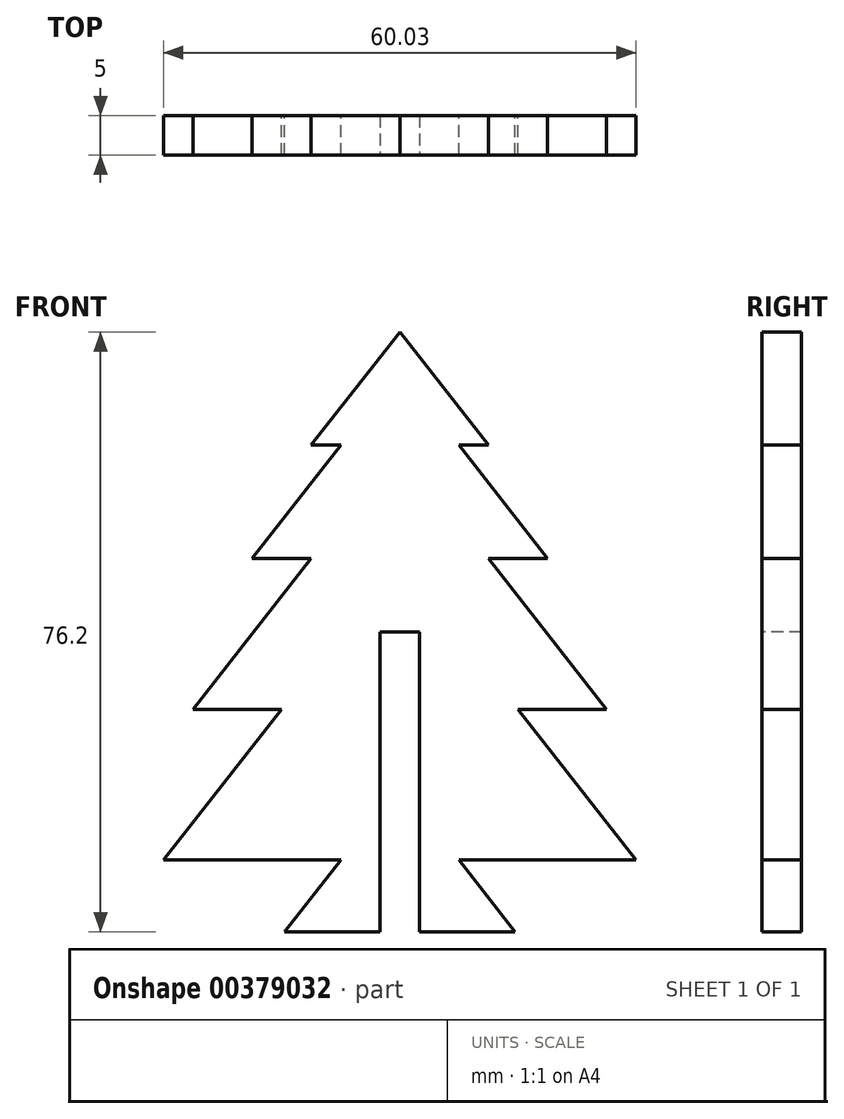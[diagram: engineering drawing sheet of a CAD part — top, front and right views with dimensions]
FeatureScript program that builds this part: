
annotation { "Feature Type Name" : "Feature", "Feature Type Description" : "" }
export const myFeature = defineFeature(function(context is Context, id is Id, definition is map)
    precondition{}
    {
        {
            var Q0;
            Q0=qCreatedBy(makeId("Front.planeOp"),FACE);
            var sketch = newSketch(context, id + "F0", { "sketchPlane" : qUnion([Q0])});
            skLineSegment(sketch, "E0", {"start": v(-37.98, -13.58) * mm, "end": v(-30.48, -13.58) * mm});
            skLineSegment(sketch, "E1", {"start": v(-30.48, -13.58) * mm, "end": v(-45.49, -13.58) * mm});
            skLineSegment(sketch, "E2", {"start": v(-45.49, -13.58) * mm, "end": v(-45.49, -4.45) * mm});
            skLineSegment(sketch, "E3", {"start": v(-30.48, -4.45) * mm, "end": v(-45.49, -4.45) * mm});
            skLineSegment(sketch, "E4", {"start": v(-30.48, -4.45) * mm, "end": v(-30.48, -13.58) * mm});
            skLineSegment(sketch, "E5", {"start": v(-37.98, -13.58) * mm, "end": v(-37.98, -4.45) * mm});
            skLineSegment(sketch, "E6", {"start": v(-45.49, -4.45) * mm, "end": v(-68, -4.45) * mm});
            skLineSegment(sketch, "E7", {"start": v(-30.48, -4.45) * mm, "end": v(-7.97, -4.45) * mm});
            skLineSegment(sketch, "E8", {"start": v(-68, -4.45) * mm, "end": v(-52.99, 14.71) * mm});
            skLineSegment(sketch, "E9", {"start": v(-52.99, 14.71) * mm, "end": v(-22.98, 14.71) * mm});
            skLineSegment(sketch, "E10", {"start": v(-22.98, 14.71) * mm, "end": v(-7.97, -4.45) * mm});
            skLineSegment(sketch, "E11", {"start": v(-37.98, -4.45) * mm, "end": v(-37.98, 14.71) * mm});
            skLineSegment(sketch, "E12", {"start": v(-52.99, 14.71) * mm, "end": v(-64.25, 14.71) * mm});
            skLineSegment(sketch, "E13", {"start": v(-64.25, 14.71) * mm, "end": v(-49.24, 33.88) * mm});
            skLineSegment(sketch, "E14", {"start": v(-22.98, 14.71) * mm, "end": v(-11.72, 14.71) * mm});
            skLineSegment(sketch, "E15", {"start": v(-11.72, 14.71) * mm, "end": v(-26.73, 33.88) * mm});
            skLineSegment(sketch, "E16", {"start": v(-26.73, 33.88) * mm, "end": v(-49.24, 33.88) * mm});
            skLineSegment(sketch, "E17", {"start": v(-37.98, 14.71) * mm, "end": v(-37.98, 33.88) * mm});
            skLineSegment(sketch, "E18", {"start": v(-49.24, 33.88) * mm, "end": v(-56.74, 33.88) * mm});
            skLineSegment(sketch, "E19", {"start": v(-56.74, 33.88) * mm, "end": v(-45.49, 48.25) * mm});
            skLineSegment(sketch, "E20", {"start": v(-45.49, 48.25) * mm, "end": v(-30.48, 48.25) * mm});
            skLineSegment(sketch, "E21", {"start": v(-30.48, 48.25) * mm, "end": v(-19.22, 33.88) * mm});
            skLineSegment(sketch, "E22", {"start": v(-19.22, 33.88) * mm, "end": v(-26.73, 33.88) * mm});
            skLineSegment(sketch, "E23", {"start": v(-45.49, 48.25) * mm, "end": v(-49.24, 48.25) * mm});
            skLineSegment(sketch, "E24", {"start": v(-49.24, 48.25) * mm, "end": v(-37.98, 62.62) * mm});
            skLineSegment(sketch, "E25", {"start": v(-37.98, 62.62) * mm, "end": v(-26.73, 48.25) * mm});
            skLineSegment(sketch, "E26", {"start": v(-26.73, 48.25) * mm, "end": v(-30.48, 48.25) * mm});
            skLineSegment(sketch, "E27", {"start": v(-68, -4.45) * mm, "end": v(-37.98, -4.45) * mm});
            skLineSegment(sketch, "E28", {"start": v(-37.98, -4.45) * mm, "end": v(-7.97, -4.45) * mm});
            skLineSegment(sketch, "E29", {"start": v(-45.49, -13.58) * mm, "end": v(-52.63, -13.58) * mm});
            skLineSegment(sketch, "E30", {"start": v(-52.63, -13.58) * mm, "end": v(-45.49, -4.45) * mm});
            skLineSegment(sketch, "E31", {"start": v(-30.48, -13.58) * mm, "end": v(-23.33, -13.58) * mm});
            skLineSegment(sketch, "E32", {"start": v(-23.33, -13.58) * mm, "end": v(-30.48, -4.45) * mm});
            skSolve(sketch);
        }
        {
            var Q0;
            Q0=makeQuery(id+"F0.imprint","IMPRINT",FACE,{"disambiguationData":[TD([[makeQuery(id+"F0.imprint","IMPRINT",EDGE,{"derivedFrom":sQuery(id+"F0.wireOp",EDGE,"E20")}),1.0]])]});
            var Q1;
            {var subQ0=sQuery(id+"F0.wireOp",EDGE,"E18");Q1=makeQuery(id+"F0.imprint","IMPRINT",FACE,{"disambiguationData":[TD([[makeQuery(id+"F0.imprint","IMPRINT",EDGE,{"derivedFrom":subQ0}),-1.0]])]});}
            var Q2;
            {var subQ3=sQuery(id+"F0.wireOp",EDGE,"E12");Q2=makeQuery(id+"F0.imprint","IMPRINT",FACE,{"disambiguationData":[TD([[makeQuery(id+"F0.imprint","IMPRINT",EDGE,{"derivedFrom":subQ3}),-1.0]])]});}
            var Q3;
            {var subQ3=sQuery(id+"F0.wireOp",EDGE,"E14");Q3=makeQuery(id+"F0.imprint","IMPRINT",FACE,{"disambiguationData":[TD([[makeQuery(id+"F0.imprint","IMPRINT",EDGE,{"derivedFrom":subQ3}),1.0]])]});}
            var Q4;
            {var subQ3=sQuery(id+"F0.wireOp",EDGE,"E8");Q4=makeQuery(id+"F0.imprint","IMPRINT",FACE,{"disambiguationData":[TD([[makeQuery(id+"F0.imprint","IMPRINT",EDGE,{"derivedFrom":subQ3}),-1.0]])]});}
            var Q5;
            {var subQ3=sQuery(id+"F0.wireOp",EDGE,"E10");Q5=makeQuery(id+"F0.imprint","IMPRINT",FACE,{"disambiguationData":[TD([[makeQuery(id+"F0.imprint","IMPRINT",EDGE,{"derivedFrom":subQ3}),-1.0]])]});}
            var Q6;
            Q6=makeQuery(id+"F0.imprint","IMPRINT",FACE,{"disambiguationData":[TD([[makeQuery(id+"F0.imprint","IMPRINT",EDGE,{"derivedFrom":sQuery(id+"F0.wireOp",EDGE,"E2")}),1.0]])]});
            var Q7;
            {var subQ0=sQuery(id+"F0.wireOp",EDGE,"E2");Q7=makeQuery(id+"F0.imprint","IMPRINT",FACE,{"disambiguationData":[TD([[makeQuery(id+"F0.imprint","IMPRINT",EDGE,{"derivedFrom":subQ0}),-1.0]])]});}
            var Q8;
            {var subQ0=sQuery(id+"F0.wireOp",EDGE,"E4");Q8=makeQuery(id+"F0.imprint","IMPRINT",FACE,{"disambiguationData":[TD([[makeQuery(id+"F0.imprint","IMPRINT",EDGE,{"derivedFrom":subQ0}),-1.0]])]});}
            var Q9;
            Q9=makeQuery(id+"F0.imprint","IMPRINT",FACE,{"disambiguationData":[TD([[makeQuery(id+"F0.imprint","IMPRINT",EDGE,{"derivedFrom":sQuery(id+"F0.wireOp",EDGE,"E4")}),1.0]])]});
            extrude(context, id + "F1", {"entities" : qUnion([Q0, Q1, Q2, Q3, Q4, Q5, Q6, Q7, Q8, Q9]), "depth" : 5 * mm});
        }
        {
            var Q0;
            Q0=makeQuery(id+"F1.opExtrude","CAP_FACE",FACE,{"disambiguationData":[OSD([sQuery(id+"F0.wireOp",EDGE,"E1"),sQuery(id+"F0.wireOp",EDGE,"E8"),sQuery(id+"F0.wireOp",EDGE,"E10"),sQuery(id+"F0.wireOp",EDGE,"E12"),sQuery(id+"F0.wireOp",EDGE,"E13"),sQuery(id+"F0.wireOp",EDGE,"E14"),sQuery(id+"F0.wireOp",EDGE,"E15"),sQuery(id+"F0.wireOp",EDGE,"E18"),sQuery(id+"F0.wireOp",EDGE,"E19"),sQuery(id+"F0.wireOp",EDGE,"E21"),sQuery(id+"F0.wireOp",EDGE,"E22"),sQuery(id+"F0.wireOp",EDGE,"E23"),sQuery(id+"F0.wireOp",EDGE,"E24"),sQuery(id+"F0.wireOp",EDGE,"E25"),sQuery(id+"F0.wireOp",EDGE,"E26"),sQuery(id+"F0.wireOp",EDGE,"E27"),sQuery(id+"F0.wireOp",EDGE,"E28"),sQuery(id+"F0.wireOp",EDGE,"E29"),sQuery(id+"F0.wireOp",EDGE,"E30"),sQuery(id+"F0.wireOp",EDGE,"E31"),sQuery(id+"F0.wireOp",EDGE,"E32")])],"isStart":false});
            var sketch = newSketch(context, id + "F2", { "sketchPlane" : qUnion([Q0])});
            skLineSegment(sketch, "E33", {"start": v(-37.98, -13.58) * mm, "end": v(-37.98, 24.52) * mm});
            skLineSegment(sketch, "E34.bottom", {"start": v(-35.48, -13.58) * mm, "end": v(-40.48, -13.58) * mm});
            skLineSegment(sketch, "E34.top", {"start": v(-35.48, 24.52) * mm, "end": v(-40.48, 24.52) * mm});
            skLineSegment(sketch, "E34.left", {"start": v(-35.48, -13.58) * mm, "end": v(-35.48, 24.52) * mm});
            skLineSegment(sketch, "E34.right", {"start": v(-40.48, -13.58) * mm, "end": v(-40.48, 24.52) * mm});
            skPoint(sketch, "E34.middle", {"position": v(-37.98, 5.47) * mm});
            skSolve(sketch);
        }
        {
            var Q0;
            {var subQ0=sQuery(id+"F2.wireOp",EDGE,"E33");Q0=makeQuery(id+"F2.imprint","IMPRINT",FACE,{"disambiguationData":[TD([[makeQuery(id+"F2.imprint","IMPRINT",EDGE,{"derivedFrom":subQ0}),1.0]])]});}
            var Q1;
            {var subQ0=sQuery(id+"F2.wireOp",EDGE,"E33");Q1=makeQuery(id+"F2.imprint","IMPRINT",FACE,{"disambiguationData":[TD([[makeQuery(id+"F2.imprint","IMPRINT",EDGE,{"derivedFrom":subQ0}),-1.0]])]});}
            extrude(context, id + "F3", {"entities" : qUnion([Q0, Q1]), "operationType" : NewBodyOperationType.REMOVE, "oppositeDirection" : true, "depth" : 25 * mm});
        }
    });
